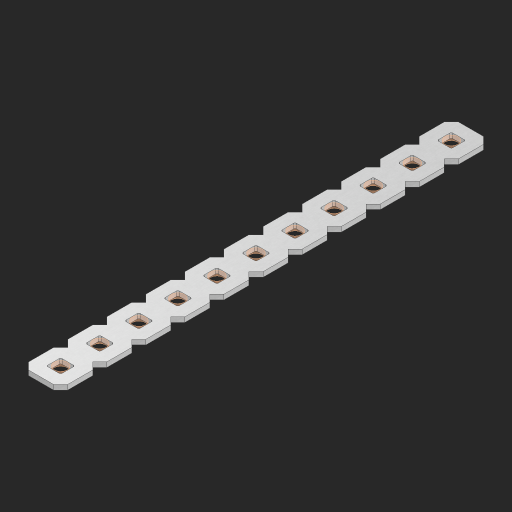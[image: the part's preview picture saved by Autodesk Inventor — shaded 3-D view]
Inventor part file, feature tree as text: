
AUTODESK INVENTOR PART (.ipt)
format: ipt  version: 2023 (Build 270158000, 158)  size: 383,488 bytes
history: native  units: in
note: dims shown in document units (in); Inventor stores cm internally (conversion verified against a paired STEP export)
features: other x12, extrude x10, sketch x2, pattern_linear x1
ambient origin geometry x8: Origin, YZ Plane, XZ Plane, XY Plane, X Axis, Y Axis, Z Axis, Center Point
bodies: Solid1 (feature_tree), Body (feature_tree)
feature tree (25):
  pattern_linear  "Rectangular Pattern1"  Spacing1=0.09in  [1 undecoded]
  sketch  "Sketch1"  dims[d1=0.5in]
  sketch  "Sketch2"  dims[d2=0.182in d3=0.09in d4=0.09in d5=0.09in d6=0.09in d7=0.09in d8=0.09in d9=0.09in d10=0.09in d11=0.02in d13=0.0in d14=0.172in d15=0.0625in d16=0.0in d19=0.5in d22=0.5in]
  other  "Srf1"
  other  "Srf126"
  other  "Srf127"
  other  "Srf128"
  other  "Srf129"
  other  "Srf130"
  other  "Srf131"
  other  "Srf250"
  other  "Srf251"
  other  "Srf252"
  other  "Srf253"
  other  "Circle"
  extrude  "ExtrusionSrf126"  Depth=0.09in
  extrude  "ExtrusionSrf127"  Depth=0.09in
  extrude  "ExtrusionSrf128"  Depth=0.09in
  extrude  "ExtrusionSrf129"  Depth=0.09in
  extrude  "ExtrusionSrf130"  Depth=0.09in
  extrude  "ExtrusionSrf131"  Depth=0.09in
  extrude  "ExtrusionSrf250"  Depth=0.09in
  extrude  "ExtrusionSrf251"  Depth=0.02in
  extrude  "ExtrusionSrf252"  TaperAngle=0.0deg  [1 undecoded]
  extrude  "ExtrusionSrf253"  Depth=0.5in
note: 2 required parameter values undecoded (feature->parameter linkage not recoverable at this tier; creation-order binding heuristic only, values carry confidence <= 0.55)
